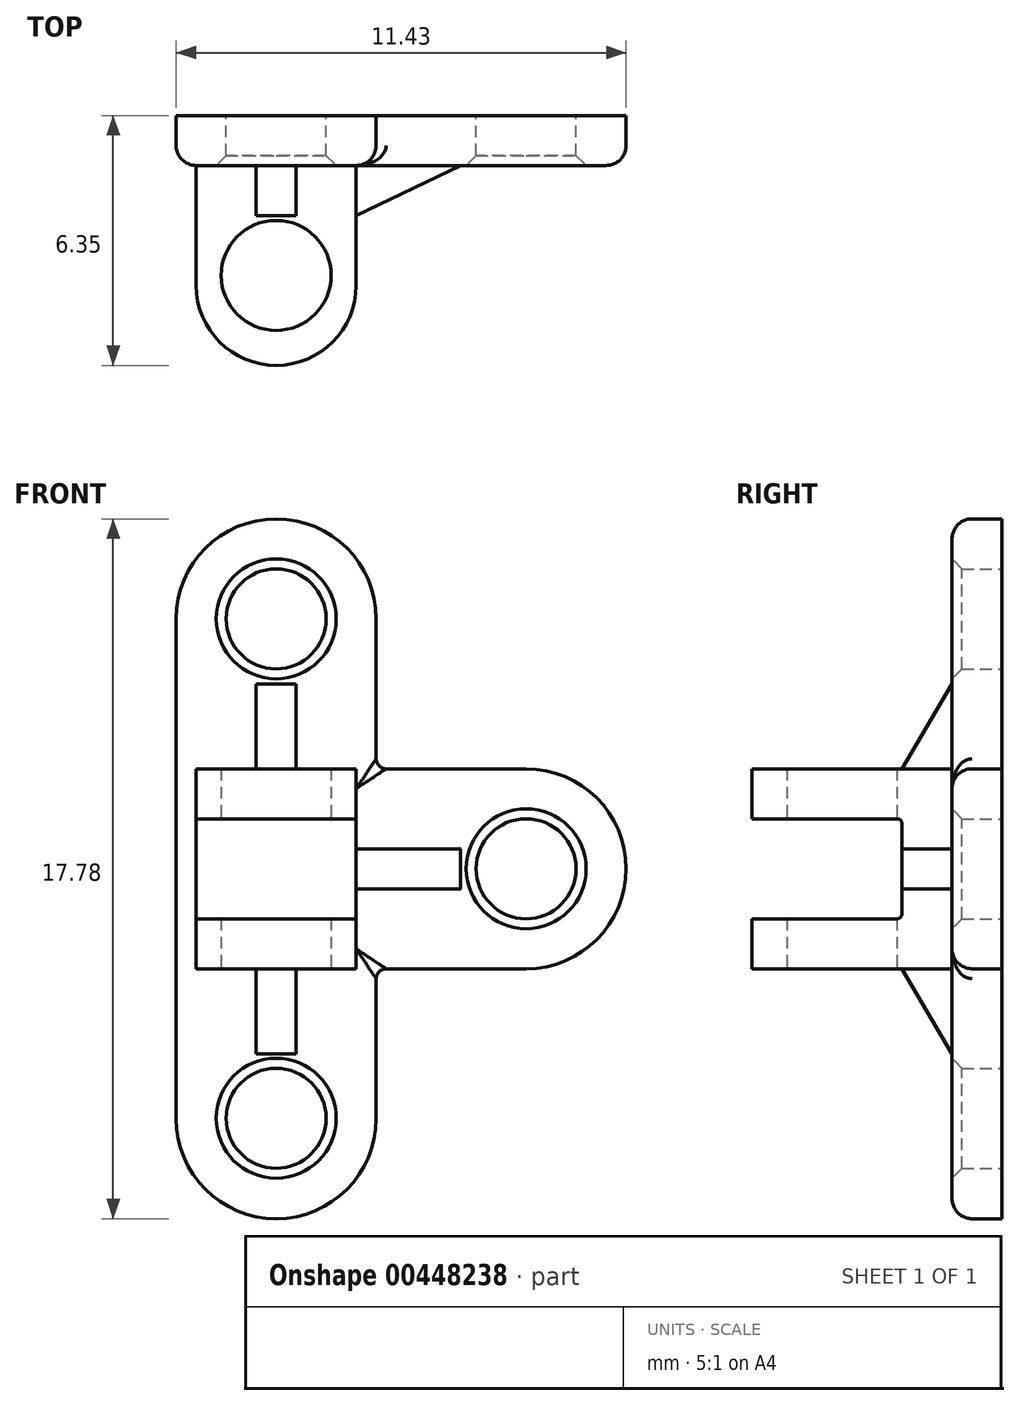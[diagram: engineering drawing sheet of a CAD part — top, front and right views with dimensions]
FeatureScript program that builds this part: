
annotation { "Feature Type Name" : "Feature", "Feature Type Description" : "" }
export const myFeature = defineFeature(function(context is Context, id is Id, definition is map)
    precondition{}
    {
        {
            var Q0;
            Q0=qCreatedBy(makeId("Front.planeOp"),FACE);
            var sketch = newSketch(context, id + "F0", { "sketchPlane" : qUnion([Q0])});
            skLineSegment(sketch, "E0", {"start": v(-2.54, 6.35) * mm, "end": v(-2.54, -6.35) * mm});
            skLineSegment(sketch, "E1", {"start": v(2.54, -6.35) * mm, "end": v(2.54, -2.54) * mm});
            skLineSegment(sketch, "E2", {"start": v(2.54, -2.54) * mm, "end": v(6.35, -2.54) * mm});
            skLineSegment(sketch, "E3", {"start": v(6.35, 2.54) * mm, "end": v(2.54, 2.54) * mm});
            skLineSegment(sketch, "E4", {"start": v(2.54, 2.54) * mm, "end": v(2.54, 6.35) * mm});
            skArc(sketch, "E5", {"start": v(2.54, 6.35) * mm, "mid": v(0, 8.9) * mm, "end": v(-2.54, 6.35) * mm});
            skArc(sketch, "E6", {"start": v(-2.54, -6.35) * mm, "mid": v(0, -8.9) * mm, "end": v(2.54, -6.35) * mm});
            skArc(sketch, "E7", {"start": v(6.35, -2.54) * mm, "mid": v(8.9, 0) * mm, "end": v(6.35, 2.54) * mm});
            skLineSegment(sketch, "E8", {"start": v(0, 6.35) * mm, "end": v(0, -6.35) * mm, "construction": true});
            skSolve(sketch);
        }
        {
            var Q0;
            Q0 = qSketchRegion(id + "F0", true);
            extrude(context, id + "F1", {"entities" : qUnion([Q0]), "depth" : 1.27 * mm});
        }
        {
            var Q0;
            Q0=makeQuery(id+"F1.opExtrude","CAP_EDGE",EDGE,{"disambiguationData":[OSD([sQuery(id+"F0.wireOp",EDGE,"E0")])],"isStart":false});
            var Q1;
            Q1=makeQuery(id+"F1.opExtrude","CAP_EDGE",EDGE,{"disambiguationData":[OSD([sQuery(id+"F0.wireOp",EDGE,"E5")])],"isStart":false});
            var Q2;
            Q2=makeQuery(id+"F1.opExtrude","CAP_EDGE",EDGE,{"disambiguationData":[OSD([sQuery(id+"F0.wireOp",EDGE,"E4")])],"isStart":false});
            var Q3;
            Q3=makeQuery(id+"F1.opExtrude","CAP_EDGE",EDGE,{"disambiguationData":[OSD([sQuery(id+"F0.wireOp",EDGE,"E3")])],"isStart":false});
            var Q4;
            Q4=makeQuery(id+"F1.opExtrude","CAP_EDGE",EDGE,{"disambiguationData":[OSD([sQuery(id+"F0.wireOp",EDGE,"E7")])],"isStart":false});
            var Q5;
            Q5=makeQuery(id+"F1.opExtrude","CAP_EDGE",EDGE,{"disambiguationData":[OSD([sQuery(id+"F0.wireOp",EDGE,"E2")])],"isStart":false});
            var Q6;
            Q6=makeQuery(id+"F1.opExtrude","CAP_EDGE",EDGE,{"disambiguationData":[OSD([sQuery(id+"F0.wireOp",EDGE,"E1")])],"isStart":false});
            var Q7;
            Q7=makeQuery(id+"F1.opExtrude","CAP_EDGE",EDGE,{"disambiguationData":[OSD([sQuery(id+"F0.wireOp",EDGE,"E6")])],"isStart":false});
            fillet(context, id + "F2", {"entities" : qUnion([Q0, Q1, Q2, Q3, Q4, Q5, Q6, Q7]), "radius" : 0.5 * mm, "tangentPropagation" : true, "allowEdgeOverflow" : false});
        }
        {
            var Q0;
            Q0=qCreatedBy(makeId("Front.planeOp"),FACE);
            var sketch = newSketch(context, id + "F3", { "sketchPlane" : qUnion([Q0])});
            skCircle(sketch, "E9", {"center": v(0, 6.35) * mm, "radius": 1.27 * mm});
            skCircle(sketch, "E10", {"center": v(0, -6.34) * mm, "radius": 1.27 * mm});
            skCircle(sketch, "E11", {"center": v(6.35, 0) * mm, "radius": 1.27 * mm});
            skSolve(sketch);
        }
        {
            var Q0;
            Q0 = qSketchRegion(id + "F3", true);
            extrude(context, id + "F4", {"entities" : qUnion([Q0]), "operationType" : NewBodyOperationType.REMOVE, "depth" : 25.4 * mm});
        }
        {
            var Q0;
            Q0=makeQuery(id+"F4.boolean.opBoolean","INTERSECT",EDGE,{"derivedFrom":[makeQuery(id+"F1.opExtrude","CAP_FACE",FACE,{"disambiguationData":[OSD([sQuery(id+"F0.wireOp",EDGE,"E0"),sQuery(id+"F0.wireOp",EDGE,"E1"),sQuery(id+"F0.wireOp",EDGE,"E2"),sQuery(id+"F0.wireOp",EDGE,"E3"),sQuery(id+"F0.wireOp",EDGE,"E4"),sQuery(id+"F0.wireOp",EDGE,"E5"),sQuery(id+"F0.wireOp",EDGE,"E6"),sQuery(id+"F0.wireOp",EDGE,"E7")])],"isStart":false}),makeQuery(id+"F4.opExtrude","SWEPT_FACE",FACE,{"disambiguationData":[OSD([sQuery(id+"F3.wireOp",EDGE,"E10")])]})]});
            var Q1;
            Q1=makeQuery(id+"F4.boolean.opBoolean","INTERSECT",EDGE,{"derivedFrom":[makeQuery(id+"F1.opExtrude","CAP_FACE",FACE,{"disambiguationData":[OSD([sQuery(id+"F0.wireOp",EDGE,"E0"),sQuery(id+"F0.wireOp",EDGE,"E1"),sQuery(id+"F0.wireOp",EDGE,"E2"),sQuery(id+"F0.wireOp",EDGE,"E3"),sQuery(id+"F0.wireOp",EDGE,"E4"),sQuery(id+"F0.wireOp",EDGE,"E5"),sQuery(id+"F0.wireOp",EDGE,"E6"),sQuery(id+"F0.wireOp",EDGE,"E7")])],"isStart":false}),makeQuery(id+"F4.opExtrude","SWEPT_FACE",FACE,{"disambiguationData":[OSD([sQuery(id+"F3.wireOp",EDGE,"E11")])]})]});
            var Q2;
            Q2=makeQuery(id+"F4.boolean.opBoolean","INTERSECT",EDGE,{"derivedFrom":[makeQuery(id+"F1.opExtrude","CAP_FACE",FACE,{"disambiguationData":[OSD([sQuery(id+"F0.wireOp",EDGE,"E0"),sQuery(id+"F0.wireOp",EDGE,"E1"),sQuery(id+"F0.wireOp",EDGE,"E2"),sQuery(id+"F0.wireOp",EDGE,"E3"),sQuery(id+"F0.wireOp",EDGE,"E4"),sQuery(id+"F0.wireOp",EDGE,"E5"),sQuery(id+"F0.wireOp",EDGE,"E6"),sQuery(id+"F0.wireOp",EDGE,"E7")])],"isStart":false}),makeQuery(id+"F4.opExtrude","SWEPT_FACE",FACE,{"disambiguationData":[OSD([sQuery(id+"F3.wireOp",EDGE,"E9")])]})]});
            chamfer(context, id + "F5", {"entities" : qUnion([Q0, Q1, Q2]), "width" : 0.25 * mm, "tangentPropagation" : true});
        }
        {
            var Q0;
            Q0=qCreatedBy(makeId("Front.planeOp"),FACE);
            var sketch = newSketch(context, id + "F6", { "sketchPlane" : qUnion([Q0])});
            skLineSegment(sketch, "E12.bottom", {"start": v(-2.03, 2.54) * mm, "end": v(2.03, 2.54) * mm});
            skLineSegment(sketch, "E12.top", {"start": v(-2.03, -2.54) * mm, "end": v(2.03, -2.54) * mm});
            skLineSegment(sketch, "E12.left", {"start": v(-2.03, 2.54) * mm, "end": v(-2.03, -2.54) * mm});
            skLineSegment(sketch, "E12.right", {"start": v(2.03, 2.54) * mm, "end": v(2.03, -2.54) * mm});
            skSolve(sketch);
        }
        {
            var Q0;
            Q0 = qSketchRegion(id + "F6", true);
            extrude(context, id + "F7", {"entities" : qUnion([Q0]), "operationType" : NewBodyOperationType.ADD, "depth" : 2.54 * mm});
        }
        {
            var Q0;
            Q0=makeQuery(id+"F2.opFillet","BLEND_EDGE",EDGE,{"blendedFrom":[makeQuery(id+"F1.opExtrude","CAP_EDGE",EDGE,{"disambiguationData":[OSD([sQuery(id+"F0.wireOp",EDGE,"E1")])],"isStart":false}),makeQuery(id+"F1.opExtrude","CAP_EDGE",EDGE,{"disambiguationData":[OSD([sQuery(id+"F0.wireOp",EDGE,"E2")])],"isStart":false})],"blendedInto":[]});
            var Q1;
            Q1=makeQuery(id+"F1.opExtrude","SWEPT_EDGE",EDGE,{"disambiguationData":[OSD([sQuery(id+"F0.wireOp",EDGE,"E1"),sQuery(id+"F0.wireOp",EDGE,"E2")])]});
            var Q2;
            Q2=makeQuery(id+"F1.opExtrude","SWEPT_EDGE",EDGE,{"disambiguationData":[OSD([sQuery(id+"F0.wireOp",EDGE,"E3"),sQuery(id+"F0.wireOp",EDGE,"E4")])]});
            var Q3;
            Q3=makeQuery(id+"F2.opFillet","BLEND_EDGE",EDGE,{"blendedFrom":[makeQuery(id+"F1.opExtrude","CAP_EDGE",EDGE,{"disambiguationData":[OSD([sQuery(id+"F0.wireOp",EDGE,"E3")])],"isStart":false}),makeQuery(id+"F1.opExtrude","CAP_EDGE",EDGE,{"disambiguationData":[OSD([sQuery(id+"F0.wireOp",EDGE,"E4")])],"isStart":false})],"blendedInto":[]});
            fillet(context, id + "F8", {"entities" : qUnion([Q0, Q1, Q2, Q3]), "radius" : 0.25 * mm, "tangentPropagation" : true, "allowEdgeOverflow" : false});
        }
        {
            var Q0;
            Q0=qCreatedBy(makeId("Front.planeOp"),FACE);
            var sketch = newSketch(context, id + "F9", { "sketchPlane" : qUnion([Q0])});
            skLineSegment(sketch, "E13.bottom", {"start": v(-2.03, 1.27) * mm, "end": v(2.03, 1.27) * mm});
            skLineSegment(sketch, "E13.top", {"start": v(-2.03, 2.54) * mm, "end": v(2.03, 2.54) * mm});
            skLineSegment(sketch, "E13.left", {"start": v(-2.03, 2.54) * mm, "end": v(-2.03, 1.27) * mm});
            skLineSegment(sketch, "E13.right", {"start": v(2.03, 2.54) * mm, "end": v(2.03, 1.27) * mm});
            skLineSegment(sketch, "E14.bottom", {"start": v(-2.03, -2.54) * mm, "end": v(2.03, -2.54) * mm});
            skLineSegment(sketch, "E14.top", {"start": v(-2.03, -1.27) * mm, "end": v(2.03, -1.27) * mm});
            skLineSegment(sketch, "E14.left", {"start": v(-2.03, -2.54) * mm, "end": v(-2.03, -1.27) * mm});
            skLineSegment(sketch, "E14.right", {"start": v(2.03, -2.54) * mm, "end": v(2.03, -1.27) * mm});
            skSolve(sketch);
        }
        {
            var Q0;
            Q0 = qSketchRegion(id + "F9", true);
            extrude(context, id + "F10", {"entities" : qUnion([Q0]), "operationType" : NewBodyOperationType.ADD, "depth" : 6.35 * mm});
        }
        {
            var Q0;
            Q0=qCreatedBy(makeId("Top.planeOp"),FACE);
            var sketch = newSketch(context, id + "F11", { "sketchPlane" : qUnion([Q0])});
            skCircle(sketch, "E15", {"center": v(0, -4.06) * mm, "radius": 1.4 * mm});
            skSolve(sketch);
        }
        {
            var Q0;
            Q0 = qSketchRegion(id + "F11", true);
            extrude(context, id + "F12", {"entities" : qUnion([Q0]), "operationType" : NewBodyOperationType.REMOVE, "depth" : 25.4 * mm, "hasSecondDirection" : true, "secondDirectionOppositeDirection" : true, "secondDirectionDepth" : 25.4 * mm});
        }
        {
            var Q0;
            Q0=makeQuery(id+"F10.opExtrude","CAP_EDGE",EDGE,{"disambiguationData":[OSD([sQuery(id+"F9.wireOp",EDGE,"E14.left")])],"isStart":false});
            var Q1;
            Q1=makeQuery(id+"F10.opExtrude","CAP_EDGE",EDGE,{"disambiguationData":[OSD([sQuery(id+"F9.wireOp",EDGE,"E14.right")])],"isStart":false});
            var Q2;
            Q2=makeQuery(id+"F10.opExtrude","CAP_EDGE",EDGE,{"disambiguationData":[OSD([sQuery(id+"F9.wireOp",EDGE,"E13.right")])],"isStart":false});
            var Q3;
            Q3=makeQuery(id+"F10.opExtrude","CAP_EDGE",EDGE,{"disambiguationData":[OSD([sQuery(id+"F9.wireOp",EDGE,"E13.left")])],"isStart":false});
            fillet(context, id + "F13", {"entities" : qUnion([Q0, Q1, Q2, Q3]), "radius" : 2.03 * mm, "tangentPropagation" : true, "allowEdgeOverflow" : false});
        }
        {
            var Q0;
            Q0=qCreatedBy(makeId("Right.planeOp"),FACE);
            var sketch = newSketch(context, id + "F14", { "sketchPlane" : qUnion([Q0])});
            skLineSegment(sketch, "E16", {"start": v(-1.27, 2.54) * mm, "end": v(-2.54, 2.54) * mm});
            skLineSegment(sketch, "E17", {"start": v(-2.54, 2.54) * mm, "end": v(-1.27, 4.7) * mm});
            skLineSegment(sketch, "E18", {"start": v(-1.27, 4.7) * mm, "end": v(-1.27, 2.54) * mm});
            skLineSegment(sketch, "E19", {"start": v(-1.27, -2.54) * mm, "end": v(-2.54, -2.54) * mm});
            skLineSegment(sketch, "E20", {"start": v(-2.54, -2.54) * mm, "end": v(-1.27, -4.7) * mm});
            skLineSegment(sketch, "E21", {"start": v(-1.27, -4.7) * mm, "end": v(-1.27, -2.54) * mm});
            skSolve(sketch);
        }
        {
            var Q0;
            Q0 = qSketchRegion(id + "F14", true);
            extrude(context, id + "F15", {"entities" : qUnion([Q0]), "operationType" : NewBodyOperationType.ADD, "depth" : 0.5 * mm, "hasSecondDirection" : true, "secondDirectionOppositeDirection" : true, "secondDirectionDepth" : 0.5 * mm});
        }
        {
            var Q0;
            Q0=qCreatedBy(makeId("Top.planeOp"),FACE);
            var sketch = newSketch(context, id + "F16", { "sketchPlane" : qUnion([Q0])});
            skLineSegment(sketch, "E22", {"start": v(2.03, -2.54) * mm, "end": v(2.03, -1.27) * mm});
            skLineSegment(sketch, "E23", {"start": v(2.03, -1.27) * mm, "end": v(4.7, -1.27) * mm});
            skLineSegment(sketch, "E24", {"start": v(4.7, -1.27) * mm, "end": v(2.03, -2.54) * mm});
            skSolve(sketch);
        }
        {
            var Q0;
            Q0 = qSketchRegion(id + "F16", true);
            extrude(context, id + "F17", {"entities" : qUnion([Q0]), "operationType" : NewBodyOperationType.ADD, "depth" : 0.5 * mm, "hasSecondDirection" : true, "secondDirectionOppositeDirection" : true, "secondDirectionDepth" : 0.5 * mm});
        }
        {
            var Q0;
            Q0=makeQuery(id+"F10.boolean.opBoolean","INTERSECT",EDGE,{"derivedFrom":[makeQuery(id+"F7.opExtrude","CAP_FACE",FACE,{"disambiguationData":[OSD([sQuery(id+"F6.wireOp",EDGE,"E12.bottom"),sQuery(id+"F6.wireOp",EDGE,"E12.top"),sQuery(id+"F6.wireOp",EDGE,"E12.left"),sQuery(id+"F6.wireOp",EDGE,"E12.right")])],"isStart":false}),makeQuery(id+"F10.opExtrude","SWEPT_FACE",FACE,{"disambiguationData":[OSD([sQuery(id+"F9.wireOp",EDGE,"E13.bottom")])]})]});
            var Q1;
            Q1=makeQuery(id+"F10.boolean.opBoolean","INTERSECT",EDGE,{"derivedFrom":[makeQuery(id+"F7.opExtrude","CAP_FACE",FACE,{"disambiguationData":[OSD([sQuery(id+"F6.wireOp",EDGE,"E12.bottom"),sQuery(id+"F6.wireOp",EDGE,"E12.top"),sQuery(id+"F6.wireOp",EDGE,"E12.left"),sQuery(id+"F6.wireOp",EDGE,"E12.right")])],"isStart":false}),makeQuery(id+"F10.opExtrude","SWEPT_FACE",FACE,{"disambiguationData":[OSD([sQuery(id+"F9.wireOp",EDGE,"E14.top")])]})]});
            fillet(context, id + "F18", {"entities" : qUnion([Q0, Q1]), "radius" : 0.13 * mm, "tangentPropagation" : true, "allowEdgeOverflow" : false});
        }
    });
